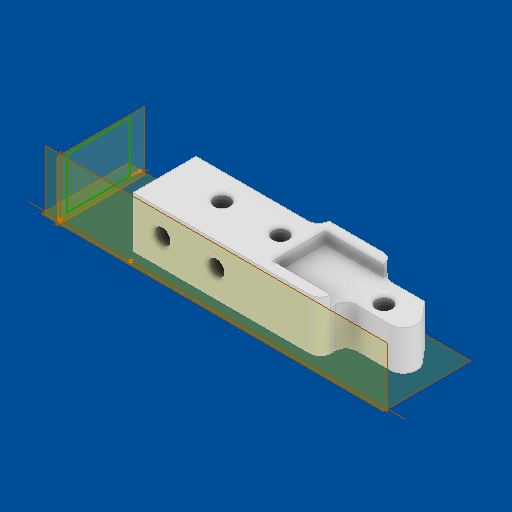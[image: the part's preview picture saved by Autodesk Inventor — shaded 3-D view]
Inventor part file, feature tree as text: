
AUTODESK INVENTOR PART (.ipt)
format: ipt  version: 2025 (Build 290162000, 162)  size: 283,136 bytes
history: native  units: in
note: dims shown in document units (in); Inventor stores cm internally (conversion verified against a paired STEP export)
features: move_body x7, direct_edit x6, sketch x6, hole x4, other x4, fillet x1, plane x1, split x1
ambient origin geometry x8: Origin, YZ Plane, XZ Plane, XY Plane, X Axis, Y Axis, Z Axis, Center Point
bodies: Solid1 (feature_tree), Body8 (feature_tree)
feature tree (30):
  direct_edit  "Direct Edit1"
  move_body  "Move Body1"
  move_body  "Move Body2"
  move_body  "Move Body3"
  move_body  "Move Body4"
  fillet  "Fillet1"  Radius=0.0962in
  sketch  "Sketch1"  dims[d0=0.0in d1=0.0in d2=0.375in d3=0.0962in]
  sketch  "Sketch2"  dims[d4=45.0deg d5=-0.875in d6=-0.375in d7=1.25in]
  plane  "Work Plane1"
  split  "Split1"
  direct_edit  "Direct Edit2"
  direct_edit  "Direct Edit3"
  direct_edit  "Direct Edit4"
  direct_edit  "Direct Edit5"
  hole  "Hole1"  [1 undecoded]
  hole  "Hole2"  [1 undecoded]
  hole  "Hole3"  [1 undecoded]
  direct_edit  "Direct Edit6"
  hole  "Hole4"  [1 undecoded]
  sketch  "Sketch3"  dims[d8=0.3937in d9=0.0in d10=0.0in d11=0.0787in d12=0.4724in]
  sketch  "Sketch4"  dims[d13=0.0in d14=0.0in d15=0.0787in d16=0.0in d17=0.0in d18=-0.006in]
  sketch  "Sketch5"  dims[d19=0.0394in d20=0.0394in]
  sketch  "Sketch6"  dims[d21=0.0394in d22=0.0968in d23=2.3622in d24=0.1575in d25=0.0787in d26=90.0deg d27=3.1811in d28=0.8108in d29=0.0968in d30=2.3622in d31=0.1575in d32=0.0787in d33=90.0deg d34=3.1811in d35=0.8108in d36=0.0968in d37=0.7874in d38=0.1575in d39=0.0787in d40=90.0deg d41=3.5433in d42=0.8108in d43=0.0394in d44=0.0968in d45=2.3622in d46=0.1575in d47=0.0787in d48=90.0deg d49=3.1811in d50=0.8108in]
  move_body  "Move1"
  move_body  "Move2"
  move_body  "Move3"
  other  "Size1"
  other  "Size2"
  other  "Size3"
  other  "Size4"
note: 4 required parameter values undecoded (feature->parameter linkage not recoverable at this tier; creation-order binding heuristic only, values carry confidence <= 0.55)
